# Revit family: Door - Internal - House van der Watt - Timber Flush Face
name_source: partatom
category: Doors
revit_build: Autodesk Revit Architecture 2012 (Build: 20110309_2315(x64)
units: mm (PartAtom-declared; Revit-internal decimal feet)

## types (2) — shared parameters
Door Leaf Depth = 42 mm
Frame Depth = 90 mm  [stored 0.295276 ft]
Frame Projection Ext. = 25 mm  [stored 0.082021 ft]
Frame Projection Int. = 25 mm  [stored 0.082021 ft]
Frame Thickness = 69 mm
Frame Thickness minus Rebate = 29 mm
Frame Width = 44 mm  [stored 0.144357 ft]
Function = Interior
Glass Inset = None
Handle Height = 1100 mm  [stored 3.60892 ft]
Rebate Depth = 44 mm  [stored 0.144357 ft]
Rebate Width = 12 mm  [stored 0.0393701 ft]
Wall Closure = By host
Width = 805 mm  [stored 2.64108 ft]

## per-type parameters (varying)
| type | Door Leaf Height | Frame Material | Height | Leaf Material |
| Door (Type 02) | 1255 mm  [stored 4.11745 ft] | SAPine - PAR - Painted Grey | 1286 mm  [stored 4.21916 ft] | SAPine - Solid Core - Painted Grey |
| Door (Type 01) | 2022 mm  [stored 6.63386 ft] | SAPine Frame - PAR - Varnished | 2053 mm  [stored 6.73556 ft] | SAPine Veneer - Solid Core - Varnished |

note: [stored X ft] marks values corroborated as IEEE doubles in the binary element streams (Revit-internal decimal feet)

## geometry (parser evidence)
native form markers: Sweep x15
no freeform markers — native parametric forms only
